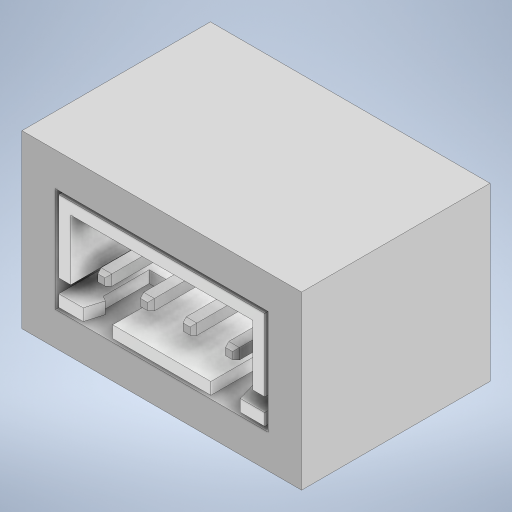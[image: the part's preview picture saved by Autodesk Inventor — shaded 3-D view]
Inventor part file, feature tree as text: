
AUTODESK INVENTOR PART (.ipt)
format: ipt  version: 2023 (Build 270158000, 158)  size: 452,096 bytes
history: native  units: mm
features: extrude x1, sketch x1, imported_body x1
ambient origin geometry x8: Origin, YZ Plane, XZ Plane, XY Plane, X Axis, Y Axis, Z Axis, Center Point
bodies: Solid1 (feature_tree), Solid2 (feature_tree)
feature tree (3):
  extrude  "Extrusion1"  Depth=2.0mm
  sketch  "Sketch1"  dims[d0=0.2mm d1=2.0mm d2=11.25mm d3=0.0mm]
  imported_body  "Base1"
